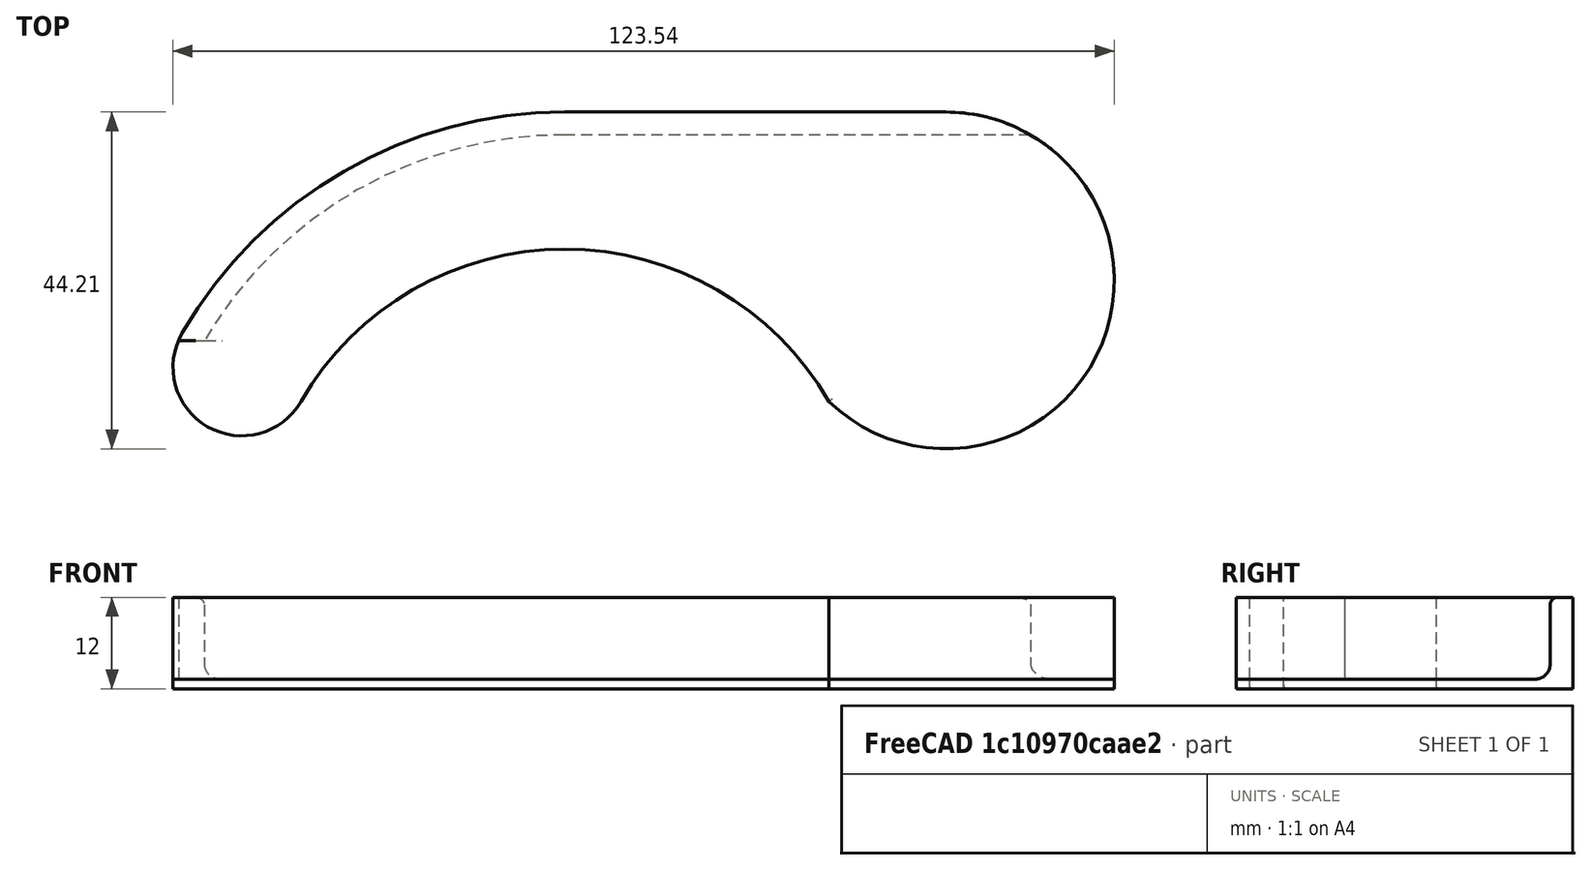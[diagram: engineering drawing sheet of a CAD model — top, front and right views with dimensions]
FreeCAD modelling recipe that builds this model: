
FCSTD DOCUMENT  (FreeCAD 0.16R)
Label: Mk1
License: All rights reserved
LicenseURL: http://en.wikipedia.org/wiki/All_rights_reserved
objects: PartDesign::Fillet×3, Sketcher::SketchObject×2, PartDesign::Pad×1, PartDesign::Pocket×1, Mesh::Feature×1
note: 9 computed .brp shape members not serialized (recipe doc carries the construction recipe); baked Part::Feature solids carry a one-line shape summary decoded from their .brp

FEATURE [Sketcher::SketchObject] Sketch
  sketch-geometry (5):
    g0: ArcOfCircle CenterX=0 CenterY=0 CenterZ=0 NormalX=0 NormalY=0 NormalZ=1 Radius=58 StartAngle=1.5708 EndAngle=2.61799
    g1: LineSegment StartX=0 StartY=58 StartZ=0 EndX=50 EndY=58 EndZ=0
    g2: ArcOfCircle CenterX=0 CenterY=0 CenterZ=0 NormalX=0 NormalY=0 NormalZ=1 Radius=40 StartAngle=0.523599 EndAngle=2.61799
    g3: ArcOfCircle CenterX=-42.4352 CenterY=24.5 CenterZ=0 NormalX=0 NormalY=0 NormalZ=1 Radius=9 StartAngle=2.61799 EndAngle=5.75958
    g4: ArcOfCircle CenterX=50 CenterY=35.8961 CenterZ=0 NormalX=0 NormalY=0 NormalZ=1 Radius=22.1039 StartAngle=3.94417 EndAngle=7.85398
  constraints (18):
    c: PointOnObject(g0,g-2)
    c: PointOnObject(g0,g-2)
    c: Radius(g0) = 58
    c: DistanceY(g0) = 58
    c: Horizontal(g1)
    c: DistanceX(g1,g1) = 50
    c: Coincident(g1,g0)
    c: Coincident(g3,g0)
    c: Coincident(g2,g3)
    c: Tangent(g3,g0)
    c: Tangent(g3,g2)
    c: DistanceY(g2) = 20
    c: Distance(g-1,g2) = 40
    c: Coincident(g2,g-1)
    c: DistanceY(g-1,g2) = 20
    c: Tangent(g4,g1)
    c: Coincident(g4,g1)
    c: Coincident(g4,g2)
FEATURE [PartDesign::Pad] Pad
  Length = 12
  Length2 = 100
  Sketch = -> Sketch
  Type = 0
FEATURE [Sketcher::SketchObject] Sketch001
  Placement = pos=(0,0,12) rot=(0,0,1;0rad)
  Support = -> Pad [Face7]
  sketch-geometry (6):
    g0: LineSegment StartX=-5.6e-05 StartY=55 StartZ=0 EndX=90 EndY=55 EndZ=0
    g1: LineSegment StartX=-60.085 StartY=0 StartZ=0 EndX=90 EndY=0 EndZ=0
    g2: LineSegment StartX=90 StartY=0 StartZ=0 EndX=90 EndY=55 EndZ=0
    g3: ArcOfCircle CenterX=1.7e-11 CenterY=2.9e-11 CenterZ=0 NormalX=0 NormalY=0 NormalZ=1 Radius=55 StartAngle=1.5708 EndAngle=2.60746
    g4: LineSegment StartX=-60.085 StartY=28 StartZ=0 EndX=-47.3392 EndY=28 EndZ=0
    g5: LineSegment StartX=-60.085 StartY=28 StartZ=0 EndX=-60.085 EndY=0 EndZ=0
  constraints (19):
    c: DistanceY(g3) = 28
    c: Distance(g-1,g3) = 55
    c: DistanceX(g0) = 90
    c: Coincident(g1,g2)
    c: Vertical(g2)
    c: Coincident(g2,g0)
    c: Horizontal(g1)
    c: Coincident(g3,g0)
    c: Radius(g3) = 55
    c: DistanceY(g1) = 0
    c: DistanceY(g2,g2) = 55
    c: DistanceY(g0) = 55
    c: DistanceX(g0) = -5.6e-05
    c: Horizontal(g4)
    c: Vertical(g5)
    c: Coincident(g1,g5)
    c: Coincident(g5,g4)
    c: Coincident(g4,g3)
    c: Distance(g1) = 150.085
FEATURE [PartDesign::Pocket] Pocket
  Length = 10.75
  Sketch = -> Sketch001
  Type = 0
FEATURE [PartDesign::Fillet] Fillet
  Base = -> Pocket [Edge20]
  Radius = 2
FEATURE [PartDesign::Fillet] Fillet001
  Base = -> Fillet [Edge24]
  Radius = 0.55
FEATURE [PartDesign::Fillet] Fillet002
  Base = -> Fillet001 [Edge15]
  Radius = 1
FEATURE [Mesh::Feature] Mesh  label="Fillet002 (Meshed)"
